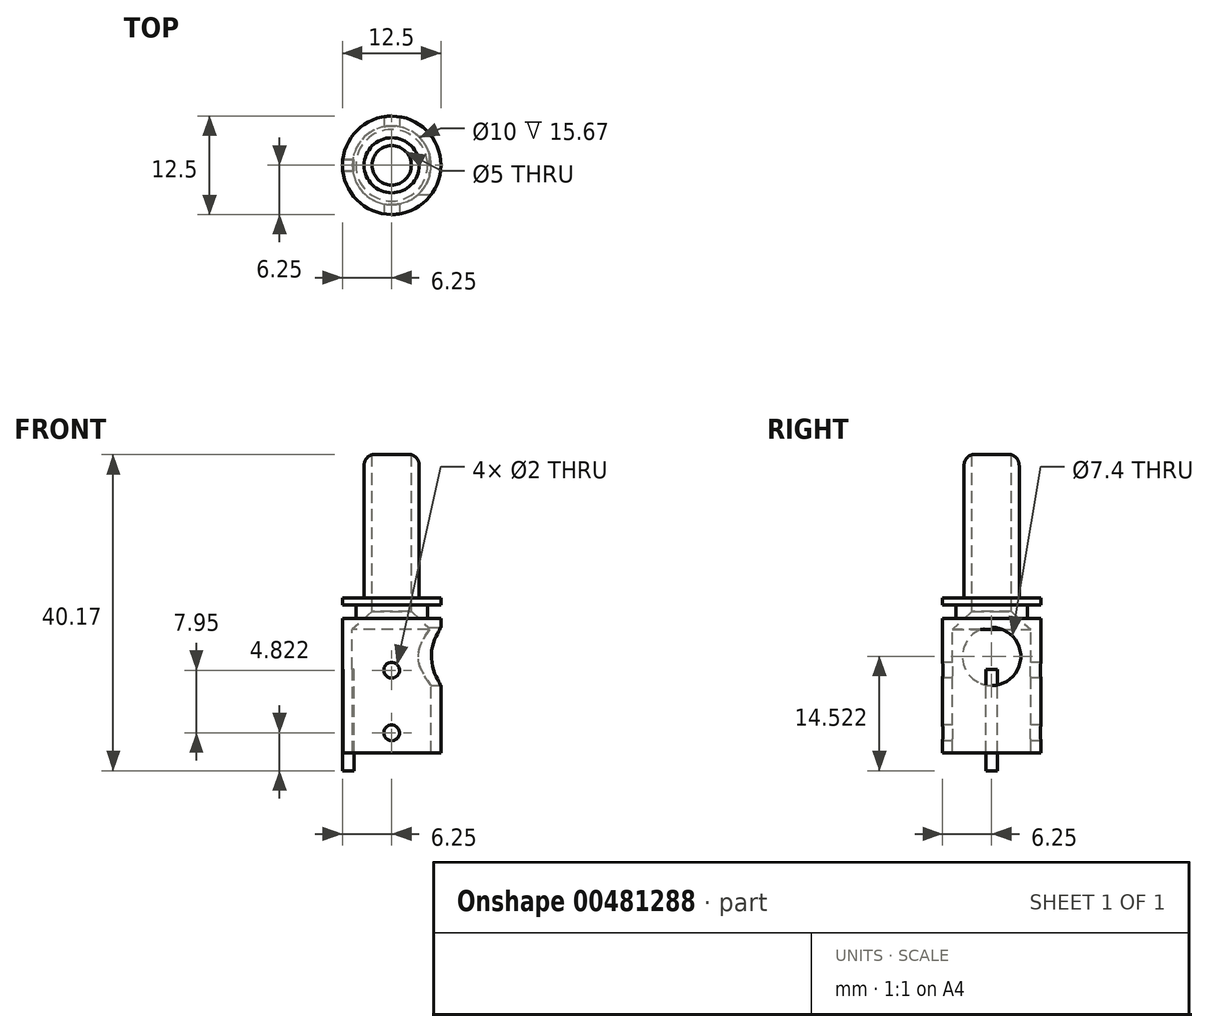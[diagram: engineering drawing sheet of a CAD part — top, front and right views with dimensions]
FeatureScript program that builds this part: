
annotation { "Feature Type Name" : "Feature", "Feature Type Description" : "" }
export const myFeature = defineFeature(function(context is Context, id is Id, definition is map)
    precondition{}
    {
        {
            var Q0;
            Q0=qCreatedBy(makeId("Right.planeOp"),FACE);
            var sketch = newSketch(context, id + "F0", { "sketchPlane" : qUnion([Q0])});
            skLineSegment(sketch, "E0", {"start": v(-3.5, 27.27) * mm, "end": v(-3.5, 9.07) * mm});
            skLineSegment(sketch, "E1", {"start": v(-3.5, 9.07) * mm, "end": v(-6.25, 9.07) * mm});
            skLineSegment(sketch, "E2", {"start": v(-6.25, 9.07) * mm, "end": v(-6.25, 8.19) * mm});
            skLineSegment(sketch, "E3", {"start": v(-6.25, 8.19) * mm, "end": v(-4.55, 8.19) * mm});
            skLineSegment(sketch, "E4", {"start": v(-4.55, 8.19) * mm, "end": v(-4.55, 6.49) * mm});
            skLineSegment(sketch, "E5", {"start": v(-4.55, 6.49) * mm, "end": v(-6.25, 6.49) * mm});
            skLineSegment(sketch, "E6", {"start": v(-6.25, 6.49) * mm, "end": v(-6.25, 5.04) * mm});
            skLineSegment(sketch, "E7", {"start": v(-6.25, 5.04) * mm, "end": v(-6.25, -10.63) * mm});
            skLineSegment(sketch, "E8", {"start": v(-6.25, -10.63) * mm, "end": v(-5, -10.63) * mm});
            skLineSegment(sketch, "E9", {"start": v(-5, -10.63) * mm, "end": v(-5, 5.04) * mm});
            skLineSegment(sketch, "E10", {"start": v(-2.5, 27.27) * mm, "end": v(-3.5, 27.27) * mm});
            skLineSegment(sketch, "E11", {"start": v(0, 37.7) * mm, "end": v(0, -24.8) * mm});
            skLineSegment(sketch, "E12", {"start": v(-5, 5.04) * mm, "end": v(-2.5, 7.34) * mm});
            skPoint(sketch, "E12.endSnap0", {"position": v(-4.55, 7.34) * mm});
            skLineSegment(sketch, "E13", {"start": v(-2.5, 27.27) * mm, "end": v(-2.5, 7.34) * mm});
            skSolve(sketch);
        }
        {
            var Q0;
            Q0 = qSketchRegion(id + "F0", true);
            var Q1;
            Q1=sQuery(id+"F0.wireOp",EDGE,"E11");
            revolve(context, id + "F1", {"entities" : qUnion([Q0]), "axis" : qUnion([Q1]), "revolveType" : RevolveType.FULL});
        }
        {
            var Q0;
            Q0=makeQuery(id+"F1.opRevolve","SWEPT_EDGE",EDGE,{"disambiguationData":[OSD([sQuery(id+"F0.wireOp",EDGE,"E0"),sQuery(id+"F0.wireOp",EDGE,"E10")])]});
            fillet(context, id + "F2", {"entities" : qUnion([Q0]), "radius" : 1.45 * mm, "tangentPropagation" : true, "allowEdgeOverflow" : false});
        }
        {
            var Q0;
            Q0=qCreatedBy(makeId("Right.planeOp"),FACE);
            cPlane(context, id + "F3", {"entities" : qUnion([Q0]), "cplaneType" : CPlaneType.OFFSET, "offset" : 7.4 * mm, "width" : 150 * mm, "height" : 150 * mm});
        }
        {
            var Q0;
            Q0=qCreatedBy(id+"F3.planeOp",FACE);
            var sketch = newSketch(context, id + "F4", { "sketchPlane" : qUnion([Q0])});
            skCircle(sketch, "E14", {"center": v(0, 1.62) * mm, "radius": 3.75 * mm});
            skSolve(sketch);
        }
        {
            var Q0;
            Q0=sQuery(id+"F4.wireOp",VERTEX,"E14.center");
            var Q1;
            Q1=makeQuery(id+"F1.opRevolve","SWEPT_BODY",BODY,{"disambiguationData":[OSD([sQuery(id+"F0.wireOp",EDGE,"E0"),sQuery(id+"F0.wireOp",EDGE,"E1"),sQuery(id+"F0.wireOp",EDGE,"E2"),sQuery(id+"F0.wireOp",EDGE,"E3"),sQuery(id+"F0.wireOp",EDGE,"E4"),sQuery(id+"F0.wireOp",EDGE,"E5"),sQuery(id+"F0.wireOp",EDGE,"E6"),sQuery(id+"F0.wireOp",EDGE,"E7"),sQuery(id+"F0.wireOp",EDGE,"E8"),sQuery(id+"F0.wireOp",EDGE,"E9"),sQuery(id+"F0.wireOp",EDGE,"WFCA2PC4-JXqy-roBc-nyxn-NizF1rpwNV58"),sQuery(id+"F0.wireOp",EDGE,"tY1BsU9W-EswD-Qo8C-ngPz-wy5FB7OOdJuZ"),sQuery(id+"F0.wireOp",EDGE,"E10")])]});
            hole(context, id + "F5", {"style" : HoleStyle.SIMPLE, "endStyle" : HoleEndStyle.BLIND, "holeDiameter" : 7.4 * mm, "holeDepth" : 2 * mm, "isTappedThrough" : true, "tappedDepth" : 12 * mm, "tapClearance" : 3, "locations" : qUnion([Q0]), "scope" : qUnion([Q1])});
        }
        {
            var Q0;
            Q0=qCreatedBy(makeId("Front.planeOp"),FACE);
            cPlane(context, id + "F6", {"entities" : qUnion([Q0]), "cplaneType" : CPlaneType.OFFSET, "offset" : 7.5 * mm, "width" : 150 * mm, "height" : 150 * mm});
        }
        {
            var Q0;
            Q0=qCreatedBy(id+"F6.planeOp",FACE);
            var sketch = newSketch(context, id + "F7", { "sketchPlane" : qUnion([Q0])});
            skCircle(sketch, "E15", {"center": v(0, -0.13) * mm, "radius": 1 * mm});
            skCircle(sketch, "E16", {"center": v(0, -8.08) * mm, "radius": 1 * mm});
            skSolve(sketch);
        }
        {
            var Q0;
            Q0=sQuery(id+"F7.wireOp",VERTEX,"E16.center");
            var Q1;
            Q1=sQuery(id+"F7.wireOp",VERTEX,"E15.center");
            var Q2;
            Q2=makeQuery(id+"F1.opRevolve","SWEPT_BODY",BODY,{"disambiguationData":[OSD([sQuery(id+"F0.wireOp",EDGE,"E0"),sQuery(id+"F0.wireOp",EDGE,"E1"),sQuery(id+"F0.wireOp",EDGE,"E2"),sQuery(id+"F0.wireOp",EDGE,"E3"),sQuery(id+"F0.wireOp",EDGE,"E4"),sQuery(id+"F0.wireOp",EDGE,"E5"),sQuery(id+"F0.wireOp",EDGE,"E6"),sQuery(id+"F0.wireOp",EDGE,"E7"),sQuery(id+"F0.wireOp",EDGE,"E8"),sQuery(id+"F0.wireOp",EDGE,"E9"),sQuery(id+"F0.wireOp",EDGE,"WFCA2PC4-JXqy-roBc-nyxn-NizF1rpwNV58"),sQuery(id+"F0.wireOp",EDGE,"tY1BsU9W-EswD-Qo8C-ngPz-wy5FB7OOdJuZ"),sQuery(id+"F0.wireOp",EDGE,"E10")])]});
            hole(context, id + "F8", {"style" : HoleStyle.SIMPLE, "endStyle" : HoleEndStyle.THROUGH, "holeDiameter" : 2 * mm, "isTappedThrough" : true, "tappedDepth" : 12 * mm, "tapClearance" : 3, "locations" : qUnion([Q0, Q1]), "scope" : qUnion([Q2])});
        }
        {
            var Q0;
            Q0=qCreatedBy(makeId("Right.planeOp"),FACE);
            cPlane(context, id + "F9", {"entities" : qUnion([Q0]), "cplaneType" : CPlaneType.OFFSET, "offset" : 6.27 * mm, "oppositeDirection" : true, "width" : 150 * mm, "height" : 150 * mm});
        }
        {
            var Q0;
            Q0=qCreatedBy(id+"F9.planeOp",FACE);
            var sketch = newSketch(context, id + "F10", { "sketchPlane" : qUnion([Q0])});
            skLineSegment(sketch, "E17", {"start": v(0.73, -10.63) * mm, "end": v(0.73, -12.33) * mm});
            skLineSegment(sketch, "E18", {"start": v(0.73, -12.33) * mm, "end": v(-0.77, -12.33) * mm});
            skLineSegment(sketch, "E19", {"start": v(-0.77, -12.33) * mm, "end": v(-0.77, -10.63) * mm});
            skLineSegment(sketch, "E20", {"start": v(-0.77, -10.63) * mm, "end": v(0.73, -10.63) * mm});
            skSolve(sketch);
        }
        {
            var Q0;
            Q0=makeQuery(id+"F10.imprint","IMPRINT",FACE,{"disambiguationData":[TD([[makeQuery(id+"F10.imprint","IMPRINT",EDGE,{"derivedFrom":sQuery(id+"F10.wireOp",EDGE,"E17")}),-1.0]])]});
            extrude(context, id + "F11", {"entities" : qUnion([Q0]), "depth" : 1.8 * mm});
        }
        {
            var Q0;
            Q0=makeQuery(id+"F11.opExtrude","SWEPT_BODY",BODY,{"disambiguationData":[OSD([sQuery(id+"F10.wireOp",EDGE,"E17"),sQuery(id+"F10.wireOp",EDGE,"E18"),sQuery(id+"F10.wireOp",EDGE,"E19"),sQuery(id+"F10.wireOp",EDGE,"E20")])]});
            deleteBodies(context, id + "F12", {"entities" : qUnion([Q0])});
        }
        {
            var Q0;
            Q0=qCreatedBy(makeId("Top.planeOp"),FACE);
            var sketch = newSketch(context, id + "F13", { "sketchPlane" : qUnion([Q0])});
            skLineSegment(sketch, "E21.bottom", {"start": v(-4.75, -0.75) * mm, "end": v(-6.25, -0.75) * mm});
            skLineSegment(sketch, "E21.top", {"start": v(-4.75, 0.75) * mm, "end": v(-6.25, 0.75) * mm});
            skLineSegment(sketch, "E21.left", {"start": v(-4.75, -0.75) * mm, "end": v(-4.75, 0.75) * mm});
            skLineSegment(sketch, "E21.right", {"start": v(-6.25, -0.75) * mm, "end": v(-6.25, 0.75) * mm});
            skPoint(sketch, "E21.middle", {"position": v(-5.5, 0) * mm});
            skSolve(sketch);
        }
        {
            var Q0;
            Q0 = qSketchRegion(id + "F13", true);
            extrude(context, id + "F14", {"entities" : qUnion([Q0]), "operationType" : NewBodyOperationType.ADD, "oppositeDirection" : true, "depth" : 12.9 * mm});
        }
    });
